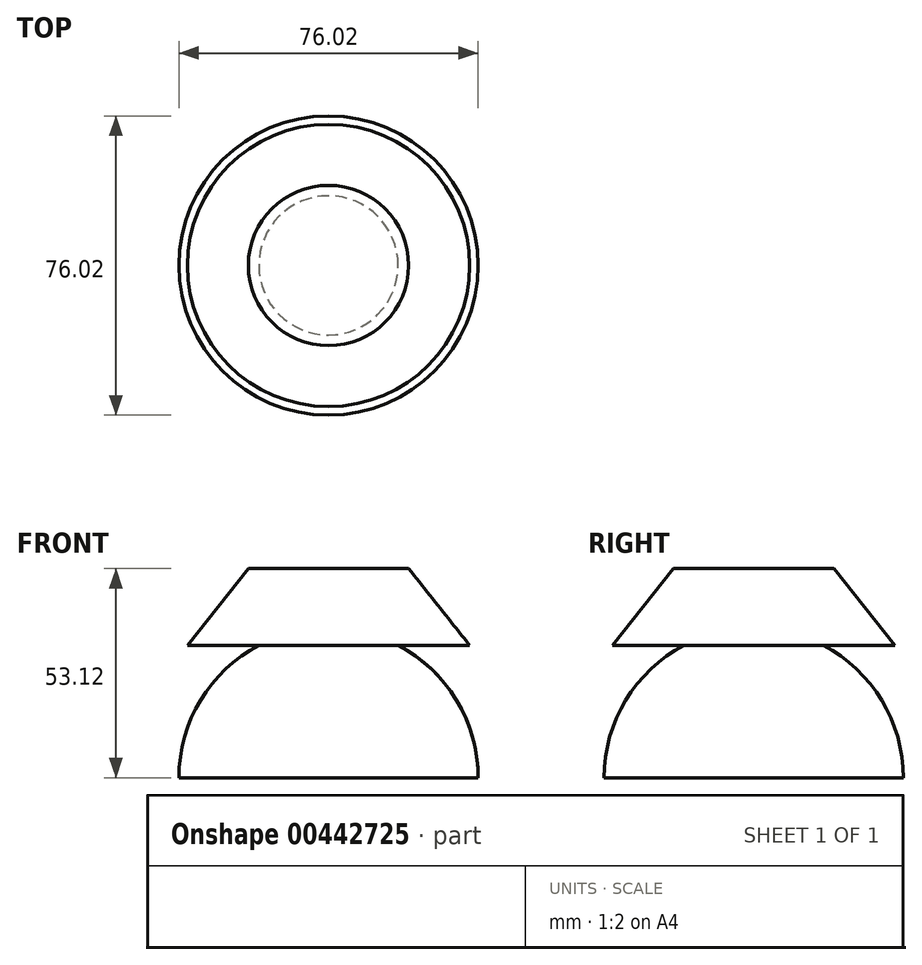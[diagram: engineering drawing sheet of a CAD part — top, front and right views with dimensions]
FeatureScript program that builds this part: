
annotation { "Feature Type Name" : "Feature", "Feature Type Description" : "" }
export const myFeature = defineFeature(function(context is Context, id is Id, definition is map)
    precondition{}
    {
        {
            var Q0;
            Q0=qCreatedBy(makeId("Front.planeOp"),FACE);
            var sketch = newSketch(context, id + "F0", { "sketchPlane" : qUnion([Q0])});
            skLineSegment(sketch, "E0", {"start": v(0, 53.12) * mm, "end": v(-20.36, 53.12) * mm});
            skLineSegment(sketch, "E1", {"start": v(-20.36, 53.12) * mm, "end": v(-35.85, 33.64) * mm});
            skLineSegment(sketch, "E2", {"start": v(-35.85, 33.64) * mm, "end": v(-17.69, 33.64) * mm});
            skArc(sketch, "E3", {"start": v(-17.69, 33.64) * mm, "mid": v(-32.53, 19.65) * mm, "end": v(-38, 0) * mm});
            skLineSegment(sketch, "E4", {"start": v(0, 0) * mm, "end": v(-38, 0) * mm});
            skPoint(sketch, "E5.orphan", {"position": v(0, 33.64) * mm});
            skLineSegment(sketch, "E6", {"start": v(0, 53.12) * mm, "end": v(0, 0) * mm});
            skSolve(sketch);
        }
        {
            var Q0;
            Q0=makeQuery(id+"F0.imprint","IMPRINT",FACE,{"disambiguationData":[TD([[makeQuery(id+"F0.imprint","IMPRINT",EDGE,{"derivedFrom":sQuery(id+"F0.wireOp",EDGE,"E0")}),1.0]])]});
            var Q1;
            Q1=sQuery(id+"F0.wireOp",EDGE,"E6");
            revolve(context, id + "F1", {"entities" : qUnion([Q0]), "axis" : qUnion([Q1]), "revolveType" : RevolveType.FULL});
        }
    });
